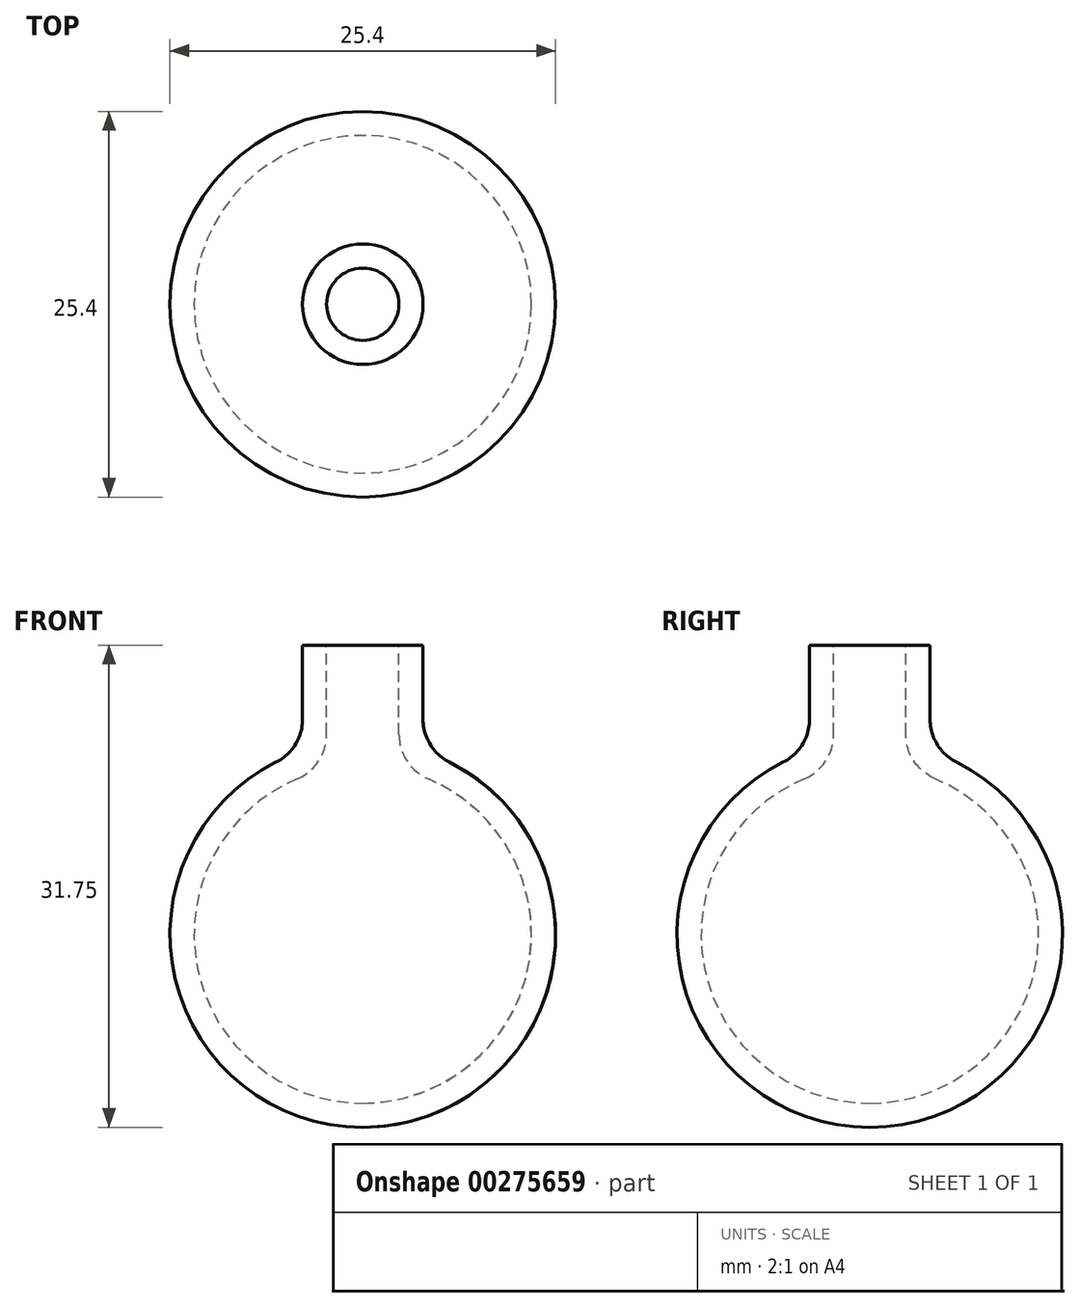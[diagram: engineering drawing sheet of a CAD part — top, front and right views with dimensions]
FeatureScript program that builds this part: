
annotation { "Feature Type Name" : "Feature", "Feature Type Description" : "" }
export const myFeature = defineFeature(function(context is Context, id is Id, definition is map)
    precondition{}
    {
        {
            var Q0;
            Q0=qCreatedBy(makeId("Front.planeOp"),FACE);
            var sketch = newSketch(context, id + "F0", { "sketchPlane" : qUnion([Q0])});
            skLineSegment(sketch, "E0", {"start": v(-3.24, 23.23) * mm, "end": v(-3.24, -44.94) * mm, "construction": true});
            skPoint(sketch, "E1.visualSharp", {"position": v(0.73, -3.96) * mm});
            skPoint(sketch, "E2.visualSharp", {"position": v(-0.85, -2.75) * mm});
            skLineSegment(sketch, "E3.MirrorCS", {"start": v(-0.85, 10.95) * mm, "end": v(0.73, 10.95) * mm});
            skLineSegment(sketch, "E4.MirrorCS", {"start": v(-3.24, -20.8) * mm, "end": v(-3.24, -19.21) * mm});
            skArc(sketch, "E5.MirrorCS", {"start": v(1.09, 2.14) * mm, "mid": v(-0.33, 3.3) * mm, "end": v(-0.85, 5.06) * mm});
            skArc(sketch, "E6.MirrorCS", {"start": v(2.48, 3.24) * mm, "mid": v(1.2, 4.41) * mm, "end": v(0.73, 6.08) * mm});
            skLineSegment(sketch, "E7.MirrorCS", {"start": v(-24.92, -4.93) * mm, "end": v(20.34, -4.93) * mm, "construction": true});
            skLineSegment(sketch, "E8.MirrorCS", {"start": v(-0.85, 5.06) * mm, "end": v(-0.85, 10.95) * mm});
            skPoint(sketch, "E9.MirrorP", {"position": v(-0.85, 2.75) * mm});
            skPoint(sketch, "E10.MirrorP", {"position": v(0.73, 3.96) * mm});
            skLineSegment(sketch, "E11.MirrorCS", {"start": v(0.73, 10.95) * mm, "end": v(0.73, 6.08) * mm});
            skLineSegment(sketch, "E12.MirrorCS", {"start": v(-25.18, -8.1) * mm, "end": v(20.4, -8.1) * mm, "construction": true});
            skArc(sketch, "E13.MirrorCS", {"start": v(2.48, 3.24) * mm, "mid": v(9.12, -11.04) * mm, "end": v(-3.24, -20.8) * mm});
            skArc(sketch, "E14.MirrorCS", {"start": v(1.09, 2.14) * mm, "mid": v(7.66, -10.3) * mm, "end": v(-3.24, -19.21) * mm});
            skSolve(sketch);
        }
        {
            var Q0;
            Q0=makeQuery(id+"F0.imprint","IMPRINT",FACE,{"disambiguationData":[TD([[makeQuery(id+"F0.imprint","IMPRINT",EDGE,{"derivedFrom":sQuery(id+"F0.wireOp",EDGE,"E3.MirrorCS")}),-1.0]])]});
            var Q1;
            Q1=sQuery(id+"F0.wireOp",EDGE,"E0");
            revolve(context, id + "F1", {"entities" : qUnion([Q0]), "axis" : qUnion([Q1]), "revolveType" : RevolveType.FULL});
        }
    });
